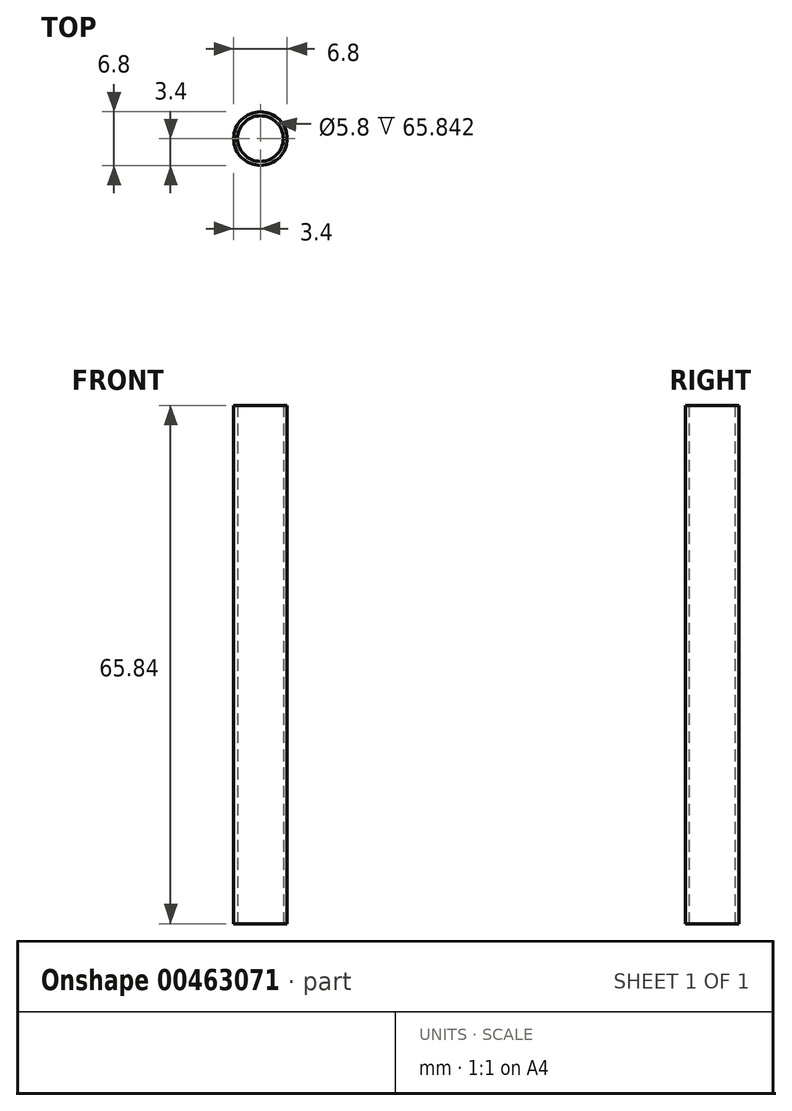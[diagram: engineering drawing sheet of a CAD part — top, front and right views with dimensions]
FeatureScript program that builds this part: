
annotation { "Feature Type Name" : "Feature", "Feature Type Description" : "" }
export const myFeature = defineFeature(function(context is Context, id is Id, definition is map)
    precondition{}
    {
        {
            var Q0;
            Q0=qCreatedBy(makeId("Top.planeOp"),FACE);
            var sketch = newSketch(context, id + "F0", { "sketchPlane" : qUnion([Q0])});
            skCircle(sketch, "E0", {"center": v(0, 0) * mm, "radius": 3.4 * mm});
            skCircle(sketch, "E1", {"center": v(0, 0) * mm, "radius": 2.9 * mm});
            skSolve(sketch);
        }
        {
            var Q0;
            Q0=makeQuery(id+"F0.imprint","IMPRINT",FACE,{"disambiguationData":[TD([[makeQuery(id+"F0.imprint","IMPRINT",EDGE,{"derivedFrom":sQuery(id+"F0.wireOp",EDGE,"E0")}),1.0]])]});
            extrude(context, id + "F1", {"entities" : qUnion([Q0]), "depth" : 65.84 * mm, "offsetDistance" : 25 * mm});
        }
    });
